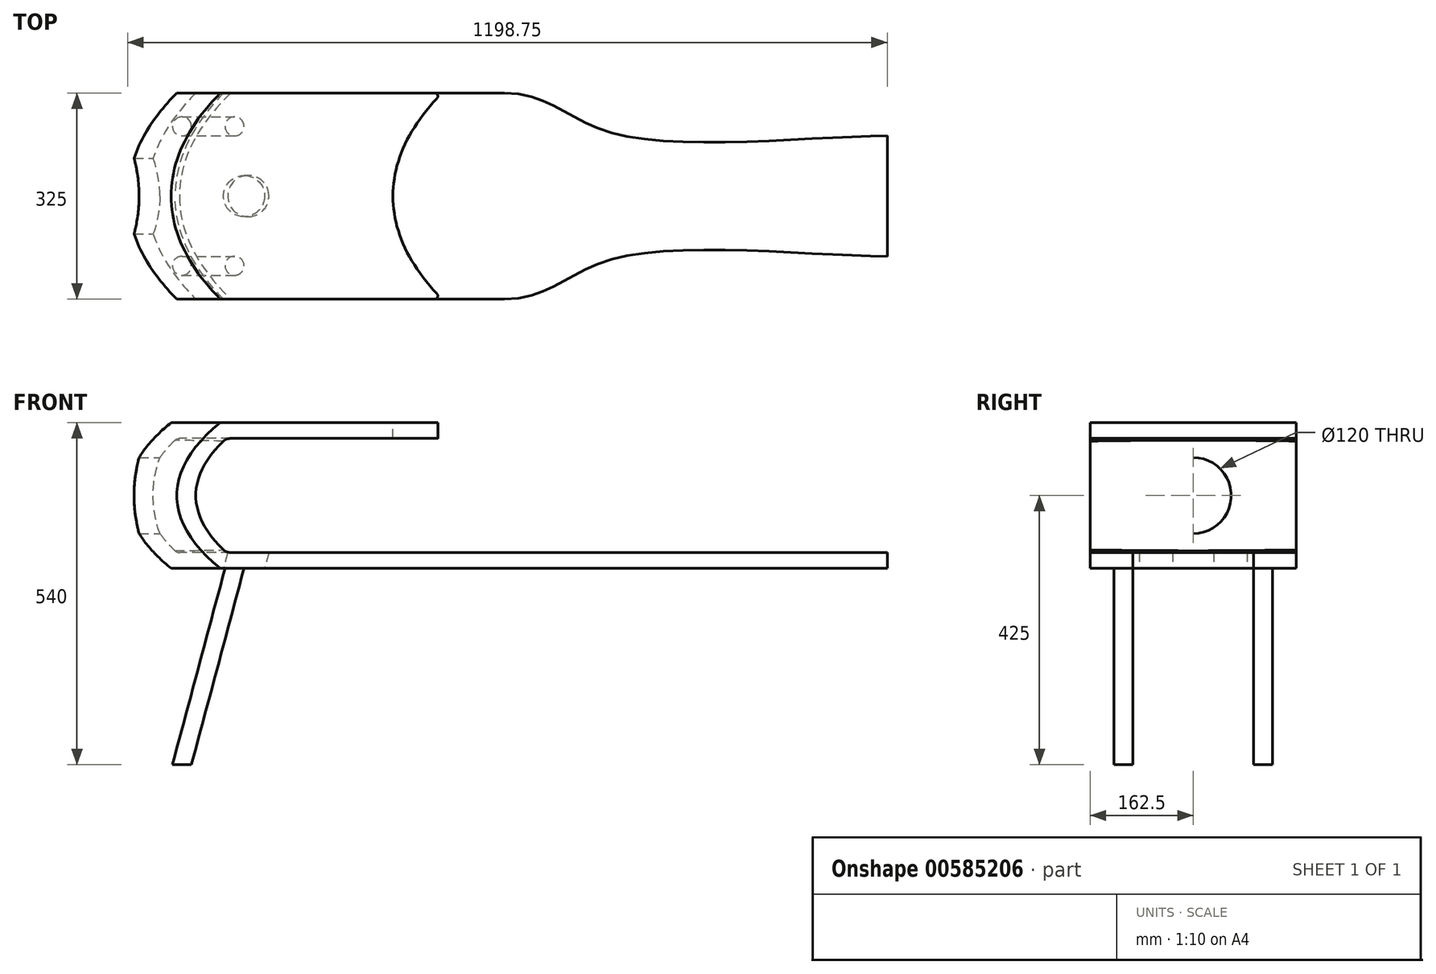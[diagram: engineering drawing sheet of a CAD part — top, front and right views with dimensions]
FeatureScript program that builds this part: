
annotation { "Feature Type Name" : "Feature", "Feature Type Description" : "" }
export const myFeature = defineFeature(function(context is Context, id is Id, definition is map)
    precondition{}
    {
        {
            var Q0;
            Q0=qCreatedBy(makeId("Front.planeOp"),FACE);
            var sketch = newSketch(context, id + "F0", { "sketchPlane" : qUnion([Q0])});
            skLineSegment(sketch, "E0", {"start": v(0, 0) * mm, "end": v(448, 0) * mm});
            skLineSegment(sketch, "E1", {"start": v(448, 25) * mm, "end": v(448, 0) * mm});
            skLineSegment(sketch, "E2", {"start": v(448, 25) * mm, "end": v(9.16, 25) * mm});
            skEllipticalArc(sketch, "E3", {});
            skEllipticalArc(sketch, "E4", {});
            skLineSegment(sketch, "E5", {"start": v(831.25, 115) * mm, "end": v(-68.75, 115) * mm, "construction": true});
            skLineSegment(sketch, "E6", {"start": v(-38.75, 115) * mm, "end": v(-68.75, 115) * mm, "construction": true});
            skLineSegment(sketch, "E7", {"start": v(831.25, 115) * mm, "end": v(831.25, -185) * mm, "construction": true});
            skLineSegment(sketch, "E8", {"start": v(831.25, -160) * mm, "end": v(831.25, -185) * mm, "construction": true});
            skLineSegment(sketch, "E9", {"start": v(0, 0) * mm, "end": v(0, 115) * mm, "construction": true});
            skLineSegment(sketch, "E10", {"start": v(0, 115) * mm, "end": v(0, 230) * mm, "construction": true});
            skLineSegment(sketch, "E11", {"start": v(0, 230) * mm, "end": v(350, 230) * mm});
            skLineSegment(sketch, "E12", {"start": v(350, 205) * mm, "end": v(350, 230) * mm});
            skLineSegment(sketch, "E13", {"start": v(350, 205) * mm, "end": v(9.16, 205) * mm});
            skLineSegment(sketch, "E14", {"start": v(831.25, 115) * mm, "end": v(657.16, -534.72) * mm});
            const initialGuessF0  = {"E3": [0.8312490601498446, 0.115, -1, 0, 0.9, 0.3, 5.889782675169492, 0.39340263201009495], "E4": [0.8312490601498446, 0.115, -1, 0, 0.87, 0.275, 5.9497693969706305, 0.3334159102089561]};
            skSetInitialGuess(sketch, initialGuessF0);
            skSolve(sketch);
        }
        {
            var Q0;
            Q0=qCreatedBy(makeId("Top.planeOp"),FACE);
            var sketch = newSketch(context, id + "F1", { "sketchPlane" : qUnion([Q0])});
            skEllipticalArc(sketch, "E15", {});
            skLineSegment(sketch, "E16", {"start": v(831.25, 0) * mm, "end": v(-68.75, 0) * mm, "construction": true});
            skLineSegment(sketch, "E17", {"start": v(831.25, 0) * mm, "end": v(831.25, 400) * mm, "construction": true});
            skLineSegment(sketch, "E18", {"start": v(8.86, 0) * mm, "end": v(8.86, 162.5) * mm, "construction": true});
            skCircle(sketch, "E19", {"center": v(115, 0) * mm, "radius": 32.5 * mm});
            skCircle(sketch, "E20", {"center": v(100, 110) * mm, "radius": 15 * mm});
            skLineSegment(sketch, "E21", {"start": v(525.61, 0) * mm, "end": v(525.61, 162.5) * mm});
            skFitSpline(sketch, "E22", {"points": [v(525.61, 162.5) * mm, v(695.61, 99.71) * mm, v(1130, 95) * mm], "startDerivative": vector(554.62, 0) * mm, "endDerivative": vector(579.63, 0) * mm});
            skLineSegment(sketch, "E23", {"start": v(525.61, 0) * mm, "end": v(1130, 0) * mm});
            skLineSegment(sketch, "E24", {"start": v(1130, 0) * mm, "end": v(1130, 95) * mm});
            skEllipticalArc(sketch, "E25.1.0.0", {});
            skLineSegment(sketch, "E25.direction1", {"start": v(-68.75, 0) * mm, "end": v(448, 0) * mm, "construction": true});
            skLineSegment(sketch, "E26", {"start": v(525.61, 162.5) * mm, "end": v(397.23, 162.5) * mm});
            skLineSegment(sketch, "E27", {"start": v(397.23, 162.5) * mm, "end": v(397.23, 0) * mm});
            skLineSegment(sketch, "E28", {"start": v(397.23, 0) * mm, "end": v(525.61, 0) * mm});
            const initialGuessF1  = {"E15": [0.8312490601498446, 0, -1, 0, 0.9, 0.4, 5.864838920736118, 0], "E25.1.0.0": [1.348, 0, -1, 0, 0.9, 0.4, 5.864838920736117, 0]};
            skSetInitialGuess(sketch, initialGuessF1);
            skSolve(sketch);
        }
        {
            var Q0;
            Q0=qCreatedBy(makeId("Front.planeOp"),FACE);
            var sketch = newSketch(context, id + "F2", { "sketchPlane" : qUnion([Q0])});
            skLineSegment(sketch, "E29", {"start": v(100, 0) * mm, "end": v(16.94, -310) * mm});
            skSolve(sketch);
        }
        {
            var Q0;
            Q0 = qSketchRegion(id + "F0", true);
            var Q1;
            Q1=sQuery(id+"F1.wireOp",EDGE,"E15");
            sweep(context, id + "F3", {"profiles" : qUnion([Q0]), "path" : qUnion([Q1]), "keepProfileOrientation" : true});
        }
        {
            var Q0;
            Q0=makeQuery(id+"F1.imprint","IMPRINT",FACE,{"disambiguationData":[TD([[makeQuery(id+"F1.imprint","IMPRINT",EDGE,{"derivedFrom":sQuery(id+"F1.wireOp",EDGE,"E20")}),1.0]])]});
            var Q1;
            Q1=sQuery(id+"F2.wireOp",EDGE,"E29");
            sweep(context, id + "F4", {"operationType" : NewBodyOperationType.ADD, "profiles" : qUnion([Q0]), "path" : qUnion([Q1])});
        }
        {
            var Q0;
            Q0=makeQuery(id+"F1.imprint","IMPRINT",FACE,{"disambiguationData":[TD([[makeQuery(id+"F1.imprint","IMPRINT",EDGE,{"derivedFrom":sQuery(id+"F1.wireOp",EDGE,"E21")}),-1.0]])]});
            var Q1;
            {var subQ0=sQuery(id+"F1.wireOp",EDGE,"E21");Q1=makeQuery(id+"F1.imprint","IMPRINT",FACE,{"disambiguationData":[TD([[makeQuery(id+"F1.imprint","IMPRINT",EDGE,{"derivedFrom":subQ0}),1.0]])]});}
            var Q2;
            {var subQ0=makeQuery(id+"F3.opSweep","SWEPT_FACE",FACE,{"disambiguationData":[OSD([sQuery(id+"F0.wireOp",EDGE,"E2"),sQuery(id+"F1.wireOp",EDGE,"E15")])]});Q2=makeQuery(id+"F6.boolean.opBoolean","MERGE",FACE,{"derivedFrom":[subQ0,makeQuery(id+"F6.opPattern","COPY",FACE,{"derivedFrom":subQ0,"instanceName":"1"})]});}
            extrude(context, id + "F5", {"entities" : qUnion([Q0, Q1]), "operationType" : NewBodyOperationType.ADD, "endBound" : BoundingType.UP_TO_SURFACE, "depth" : 25 * mm, "endBoundEntityFace" : qUnion([Q2]), "offsetDistance" : 25 * mm});
        }
        {
            var Q0;
            Q0=makeQuery(id+"F3.opSweep","SWEPT_BODY",BODY,{"disambiguationData":[OSD([sQuery(id+"F0.wireOp",EDGE,"E0"),sQuery(id+"F0.wireOp",EDGE,"E1"),sQuery(id+"F0.wireOp",EDGE,"E2"),sQuery(id+"F0.wireOp",EDGE,"E3"),sQuery(id+"F0.wireOp",EDGE,"E4"),sQuery(id+"F0.wireOp",EDGE,"E11"),sQuery(id+"F0.wireOp",EDGE,"E12"),sQuery(id+"F0.wireOp",EDGE,"E13"),sQuery(id+"F1.wireOp",EDGE,"E15")])]});
            var Q1;
            Q1=qCreatedBy(makeId("Front.planeOp"),FACE);
            mirror(context, id + "F6", {"operationType" : NewBodyOperationType.ADD, "entities" : qUnion([Q0]), "mirrorPlane" : qUnion([Q1])});
        }
        {
            var Q0;
            Q0=qCreatedBy(makeId("Right.planeOp"),FACE);
            var sketch = newSketch(context, id + "F7", { "sketchPlane" : qUnion([Q0])});
            skCircle(sketch, "E30", {"center": v(0, 115) * mm, "radius": 60 * mm});
            skSolve(sketch);
        }
        {
            var Q0;
            Q0 = qSketchRegion(id + "F7", true);
            var Q1;
            Q1=makeQuery(id+"F3.opSweep","SWEPT_FACE",FACE,{"disambiguationData":[OSD([sQuery(id+"F0.wireOp",EDGE,"E3"),sQuery(id+"F1.wireOp",EDGE,"E15")])]});
            var Q2;
            Q2=sQuery(id+"F0.wireOp",VERTEX,"E5.end");
            extrude(context, id + "F8", {"entities" : qUnion([Q0]), "operationType" : NewBodyOperationType.REMOVE, "endBound" : BoundingType.UP_TO_VERTEX, "oppositeDirection" : true, "depth" : 25 * mm, "endBoundEntityFace" : qUnion([Q1]), "endBoundEntityVertex" : qUnion([Q2]), "offsetDistance" : 25 * mm});
        }
        {
            var Q0;
            Q0=makeQuery(id+"F1.imprint","IMPRINT",FACE,{"disambiguationData":[TD([[makeQuery(id+"F1.imprint","IMPRINT",EDGE,{"derivedFrom":sQuery(id+"F1.wireOp",EDGE,"E19")}),1.0]])]});
            var Q1;
            Q1=sQuery(id+"F1.wireOp",EDGE,"E19");
            var Q2;
            Q2=sQuery(id+"F0.wireOp",EDGE,"E14");
            sweep(context, id + "F9", {"operationType" : NewBodyOperationType.REMOVE, "profiles" : qUnion([Q0]), "surfaceProfiles" : qUnion([Q1]), "path" : qUnion([Q2])});
        }
        {
            var Q0;
            Q0=makeQuery(id+"F6.opPattern","COPY",EDGE,{"derivedFrom":makeQuery(id+"F3.opSweep","SWEPT_EDGE",EDGE,{"disambiguationData":[OSD([sQuery(id+"F0.wireOp",EDGE,"E2"),sQuery(id+"F0.wireOp",EDGE,"E4"),sQuery(id+"F1.wireOp",EDGE,"E15")])]}),"instanceName":"1"});
            var Q1;
            Q1=makeQuery(id+"F3.opSweep","SWEPT_EDGE",EDGE,{"disambiguationData":[OSD([sQuery(id+"F0.wireOp",EDGE,"E2"),sQuery(id+"F0.wireOp",EDGE,"E4"),sQuery(id+"F1.wireOp",EDGE,"E15")])]});
            var Q2;
            Q2=makeQuery(id+"F3.opSweep","SWEPT_EDGE",EDGE,{"disambiguationData":[OSD([sQuery(id+"F0.wireOp",EDGE,"E4"),sQuery(id+"F0.wireOp",EDGE,"E13"),sQuery(id+"F1.wireOp",EDGE,"E15")])]});
            var Q3;
            Q3=makeQuery(id+"F6.opPattern","COPY",EDGE,{"derivedFrom":makeQuery(id+"F3.opSweep","SWEPT_EDGE",EDGE,{"disambiguationData":[OSD([sQuery(id+"F0.wireOp",EDGE,"E4"),sQuery(id+"F0.wireOp",EDGE,"E13"),sQuery(id+"F1.wireOp",EDGE,"E15")])]}),"instanceName":"1"});
            var Q4;
            Q4=makeQuery(id+"F6.opPattern","COPY",EDGE,{"derivedFrom":makeQuery(id+"F4.opSweep","CAP_EDGE",EDGE,{"disambiguationData":[OSD([sQuery(id+"F1.wireOp",EDGE,"E20"),sQuery(id+"F2.wireOp",VERTEX,"E29.start")])],"isStart":true}),"instanceName":"1"});
            var Q5;
            Q5=makeQuery(id+"F4.opSweep","CAP_EDGE",EDGE,{"disambiguationData":[OSD([sQuery(id+"F1.wireOp",EDGE,"E20"),sQuery(id+"F2.wireOp",VERTEX,"E29.start")])],"isStart":true});
            fillet(context, id + "F10", {"entities" : qUnion([Q0, Q1, Q2, Q3, Q4, Q5]), "radius" : 10 * mm, "tangentPropagation" : true, "allowEdgeOverflow" : false});
        }
        {
            var Q0;
            Q0=makeQuery(id+"F3.opSweep","CAP_EDGE",EDGE,{"disambiguationData":[OSD([sQuery(id+"F0.wireOp",EDGE,"E12"),sQuery(id+"F1.wireOp",VERTEX,"E15.start")])],"isStart":false});
            var Q1;
            Q1=makeQuery(id+"F6.opPattern","COPY",EDGE,{"derivedFrom":makeQuery(id+"F3.opSweep","CAP_EDGE",EDGE,{"disambiguationData":[OSD([sQuery(id+"F0.wireOp",EDGE,"E12"),sQuery(id+"F1.wireOp",VERTEX,"E15.start")])],"isStart":false}),"instanceName":"1"});
            fillet(context, id + "F11", {"entities" : qUnion([Q0, Q1]), "radius" : 5 * mm, "tangentPropagation" : true, "allowEdgeOverflow" : false});
        }
    });
